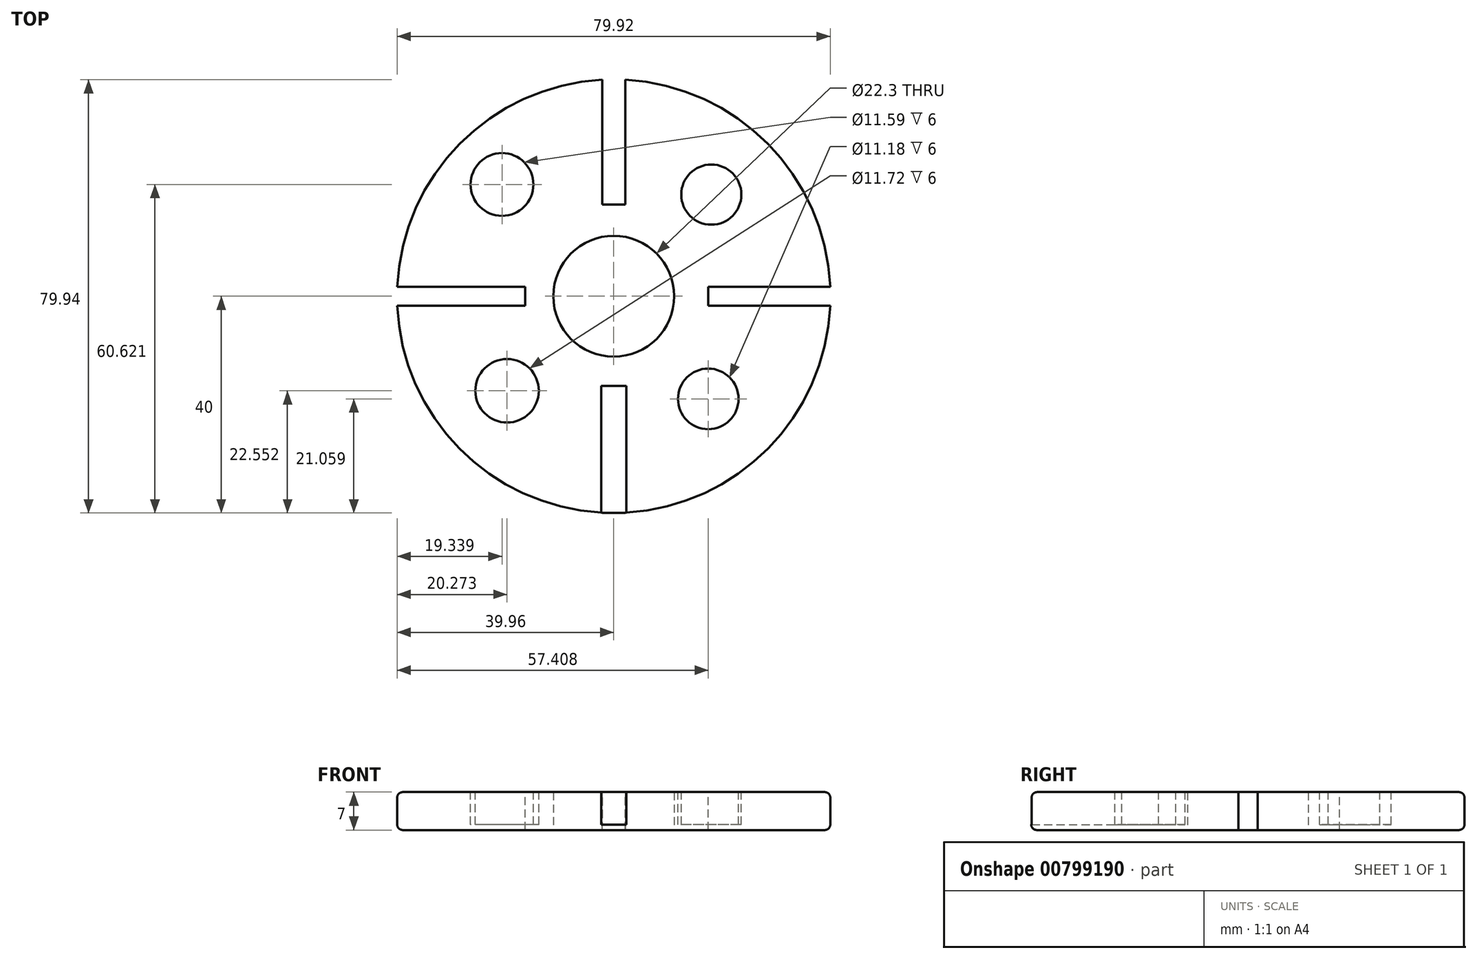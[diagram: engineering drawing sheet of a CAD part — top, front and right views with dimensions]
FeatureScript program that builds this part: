
annotation { "Feature Type Name" : "Feature", "Feature Type Description" : "" }
export const myFeature = defineFeature(function(context is Context, id is Id, definition is map)
    precondition{}
    {
        {
            var Q0;
            Q0=qCreatedBy(makeId("Top.planeOp"),FACE);
            var sketch = newSketch(context, id + "F0", { "sketchPlane" : qUnion([Q0])});
            skCircle(sketch, "E0", {"center": v(0, 0) * mm, "radius": 40 * mm});
            skCircle(sketch, "E1", {"center": v(0, 0) * mm, "radius": 11.15 * mm});
            skSolve(sketch);
        }
        {
            var Q0;
            Q0=makeQuery(id+"F0.imprint","IMPRINT",FACE,{"disambiguationData":[TD([[makeQuery(id+"F0.imprint","IMPRINT",EDGE,{"derivedFrom":sQuery(id+"F0.wireOp",EDGE,"E0")}),1.0]])]});
            extrude(context, id + "F1", {"entities" : qUnion([Q0]), "depth" : 7 * mm, "offsetDistance" : 25 * mm});
        }
        {
            var Q0;
            Q0=makeQuery(id+"F1.opExtrude","CAP_FACE",FACE,{"disambiguationData":[OSD([sQuery(id+"F0.wireOp",EDGE,"E0"),sQuery(id+"F0.wireOp",EDGE,"E1")])],"isStart":false});
            var sketch = newSketch(context, id + "F2", { "sketchPlane" : qUnion([Q0])});
            skSolve(sketch);
        }
        {
            var Q0;
            Q0=makeQuery(id+"F2.imprint","IMPRINT",FACE,{"disambiguationData":[TD([[makeQuery(id+"F2.imprint","IMPRINT",EDGE,{"derivedFrom":makeQuery(id+"F1.opExtrude","CAP_EDGE",EDGE,{"disambiguationData":[OSD([sQuery(id+"F0.wireOp",EDGE,"E0")])],"isStart":false})}),1.0]])]});
            var sketch = newSketch(context, id + "F3", { "sketchPlane" : qUnion([Q0])});
            skLineSegment(sketch, "E2.bottom", {"start": v(2.15, 16.89) * mm, "end": v(-2.15, 16.89) * mm});
            skLineSegment(sketch, "E2.top", {"start": v(2.15, 42.27) * mm, "end": v(-2.15, 42.27) * mm});
            skLineSegment(sketch, "E2.left", {"start": v(2.15, 16.89) * mm, "end": v(2.15, 42.27) * mm});
            skLineSegment(sketch, "E2.right", {"start": v(-2.15, 16.89) * mm, "end": v(-2.15, 42.27) * mm});
            skPoint(sketch, "E2.middle", {"position": v(0, 29.58) * mm});
            skSolve(sketch);
        }
        {
            var Q0;
            Q0 = qSketchRegion(id + "F3", true);
            extrude(context, id + "F4", {"entities" : qUnion([Q0]), "operationType" : NewBodyOperationType.REMOVE, "oppositeDirection" : true, "depth" : 50 * mm, "offsetDistance" : 25 * mm});
        }
        {
            var Q0;
            Q0=makeQuery(id+"F2.imprint","IMPRINT",FACE,{"disambiguationData":[TD([[makeQuery(id+"F2.imprint","IMPRINT",EDGE,{"derivedFrom":makeQuery(id+"F1.opExtrude","CAP_EDGE",EDGE,{"disambiguationData":[OSD([sQuery(id+"F0.wireOp",EDGE,"E0")])],"isStart":false})}),1.0]])]});
            var sketch = newSketch(context, id + "F5", { "sketchPlane" : qUnion([Q0])});
            skLineSegment(sketch, "E3.bottom", {"start": v(-16.33, -1.77) * mm, "end": v(-54.77, -1.77) * mm});
            skLineSegment(sketch, "E3.top", {"start": v(-16.33, 1.77) * mm, "end": v(-54.77, 1.77) * mm});
            skLineSegment(sketch, "E3.left", {"start": v(-16.33, -1.77) * mm, "end": v(-16.33, 1.77) * mm});
            skLineSegment(sketch, "E3.right", {"start": v(-54.77, -1.77) * mm, "end": v(-54.77, 1.77) * mm});
            skPoint(sketch, "E3.middle", {"position": v(-35.55, 0) * mm});
            skSolve(sketch);
        }
        {
            var Q0;
            Q0 = qSketchRegion(id + "F5", true);
            extrude(context, id + "F6", {"entities" : qUnion([Q0]), "operationType" : NewBodyOperationType.REMOVE, "oppositeDirection" : true, "depth" : 25 * mm, "offsetDistance" : 25 * mm});
        }
        {
            var Q0;
            Q0=makeQuery(id+"F2.imprint","IMPRINT",FACE,{"disambiguationData":[TD([[makeQuery(id+"F2.imprint","IMPRINT",EDGE,{"derivedFrom":makeQuery(id+"F1.opExtrude","CAP_EDGE",EDGE,{"disambiguationData":[OSD([sQuery(id+"F0.wireOp",EDGE,"E0")])],"isStart":false})}),1.0]])]});
            var sketch = newSketch(context, id + "F7", { "sketchPlane" : qUnion([Q0])});
            skLineSegment(sketch, "E4.bottom", {"start": v(2.33, -55.7) * mm, "end": v(-2.33, -55.7) * mm});
            skLineSegment(sketch, "E4.top", {"start": v(2.33, -16.52) * mm, "end": v(-2.33, -16.52) * mm});
            skLineSegment(sketch, "E4.left", {"start": v(2.33, -55.7) * mm, "end": v(2.33, -16.52) * mm});
            skLineSegment(sketch, "E4.right", {"start": v(-2.33, -55.7) * mm, "end": v(-2.33, -16.52) * mm});
            skPoint(sketch, "E4.middle", {"position": v(0, -36.1) * mm});
            skSolve(sketch);
        }
        {
            var Q0;
            Q0=makeQuery(id+"F2.imprint","IMPRINT",FACE,{"disambiguationData":[TD([[makeQuery(id+"F2.imprint","IMPRINT",EDGE,{"derivedFrom":makeQuery(id+"F1.opExtrude","CAP_EDGE",EDGE,{"disambiguationData":[OSD([sQuery(id+"F0.wireOp",EDGE,"E0")])],"isStart":false})}),1.0]])]});
            var sketch = newSketch(context, id + "F8", { "sketchPlane" : qUnion([Q0])});
            skLineSegment(sketch, "E5.bottom", {"start": v(46.93, -1.77) * mm, "end": v(17.45, -1.77) * mm});
            skLineSegment(sketch, "E5.top", {"start": v(46.93, 1.77) * mm, "end": v(17.45, 1.77) * mm});
            skLineSegment(sketch, "E5.left", {"start": v(46.93, -1.77) * mm, "end": v(46.93, 1.77) * mm});
            skLineSegment(sketch, "E5.right", {"start": v(17.45, -1.77) * mm, "end": v(17.45, 1.77) * mm});
            skPoint(sketch, "E5.middle", {"position": v(32.2, 0) * mm});
            skSolve(sketch);
        }
        {
            var Q0;
            Q0 = qSketchRegion(id + "F8", true);
            extrude(context, id + "F9", {"entities" : qUnion([Q0]), "operationType" : NewBodyOperationType.REMOVE, "oppositeDirection" : true, "depth" : 25 * mm, "offsetDistance" : 25 * mm});
        }
        {
            var Q0;
            Q0=makeQuery(id+"F2.imprint","IMPRINT",FACE,{"disambiguationData":[TD([[makeQuery(id+"F2.imprint","IMPRINT",EDGE,{"derivedFrom":makeQuery(id+"F1.opExtrude","CAP_EDGE",EDGE,{"disambiguationData":[OSD([sQuery(id+"F0.wireOp",EDGE,"E0")])],"isStart":false})}),1.0]])]});
            var sketch = newSketch(context, id + "F10", { "sketchPlane" : qUnion([Q0])});
            skCircle(sketch, "E6", {"center": v(-19.69, -17.45) * mm, "radius": 5.86 * mm});
            skCircle(sketch, "E7", {"center": v(-20.62, 20.62) * mm, "radius": 5.8 * mm});
            skSolve(sketch);
        }
        {
            var Q0;
            Q0=makeQuery(id+"F2.imprint","IMPRINT",FACE,{"disambiguationData":[TD([[makeQuery(id+"F2.imprint","IMPRINT",EDGE,{"derivedFrom":makeQuery(id+"F1.opExtrude","CAP_EDGE",EDGE,{"disambiguationData":[OSD([sQuery(id+"F0.wireOp",EDGE,"E0")])],"isStart":false})}),1.0]])]});
            var sketch = newSketch(context, id + "F11", { "sketchPlane" : qUnion([Q0])});
            skCircle(sketch, "E8", {"center": v(18, 18.75) * mm, "radius": 5.55 * mm});
            skCircle(sketch, "E9", {"center": v(17.45, -18.94) * mm, "radius": 5.6 * mm});
            skSolve(sketch);
        }
        {
            var Q0;
            {var subQ0=sQuery(id+"F0.wireOp",EDGE,"E0");Q0=makeQuery(id+"F6.boolean.opBoolean","SPLIT",EDGE,{"disambiguationData":[TD([makeQuery(id+"F4.boolean.opBoolean","COPY",FACE,{"derivedFrom":makeQuery(id+"F4.opExtrude","SWEPT_FACE",FACE,{"disambiguationData":[OSD([sQuery(id+"F3.wireOp",EDGE,"E2.right")])]})})])],"derivedFrom":makeQuery(id+"F1.opExtrude","CAP_EDGE",EDGE,{"disambiguationData":[OSD([subQ0])],"isStart":false})});}
            var Q1;
            {var subQ0=sQuery(id+"F0.wireOp",EDGE,"E0");Q1=makeQuery(id+"F6.boolean.opBoolean","SPLIT",EDGE,{"disambiguationData":[TD([makeQuery(id+"F4.boolean.opBoolean","COPY",FACE,{"derivedFrom":makeQuery(id+"F4.opExtrude","SWEPT_FACE",FACE,{"disambiguationData":[OSD([sQuery(id+"F3.wireOp",EDGE,"E2.right")])]})})])],"derivedFrom":makeQuery(id+"F1.opExtrude","CAP_EDGE",EDGE,{"disambiguationData":[OSD([subQ0])],"isStart":true})});}
            var Q2;
            {var subQ0=sQuery(id+"F0.wireOp",EDGE,"E0");var subQ3=makeQuery(id+"F4.boolean.opBoolean","COPY",FACE,{"derivedFrom":makeQuery(id+"F4.opExtrude","SWEPT_FACE",FACE,{"disambiguationData":[OSD([sQuery(id+"F3.wireOp",EDGE,"E2.left")])]})});Q2=makeQuery(id+"F9.boolean.opBoolean","SPLIT",EDGE,{"disambiguationData":[TD([subQ3])],"derivedFrom":makeQuery(id+"FT35M04vJGL3mYK_1.boolean.opBoolean","SPLIT",EDGE,{"disambiguationData":[TD([subQ3])],"derivedFrom":makeQuery(id+"F6.boolean.opBoolean","SPLIT",EDGE,{"disambiguationData":[TD([subQ3])],"derivedFrom":makeQuery(id+"F1.opExtrude","CAP_EDGE",EDGE,{"disambiguationData":[OSD([subQ0])],"isStart":true})})})});}
            var Q3;
            {var subQ0=sQuery(id+"F0.wireOp",EDGE,"E0");var subQ3=makeQuery(id+"F4.boolean.opBoolean","COPY",FACE,{"derivedFrom":makeQuery(id+"F4.opExtrude","SWEPT_FACE",FACE,{"disambiguationData":[OSD([sQuery(id+"F3.wireOp",EDGE,"E2.left")])]})});Q3=makeQuery(id+"F9.boolean.opBoolean","SPLIT",EDGE,{"disambiguationData":[TD([subQ3])],"derivedFrom":makeQuery(id+"FT35M04vJGL3mYK_1.boolean.opBoolean","SPLIT",EDGE,{"disambiguationData":[TD([subQ3])],"derivedFrom":makeQuery(id+"F6.boolean.opBoolean","SPLIT",EDGE,{"disambiguationData":[TD([subQ3])],"derivedFrom":makeQuery(id+"F1.opExtrude","CAP_EDGE",EDGE,{"disambiguationData":[OSD([subQ0])],"isStart":false})})})});}
            var Q4;
            {var subQ0=sQuery(id+"F0.wireOp",EDGE,"E0");var subQ2=makeQuery(id+"FT35M04vJGL3mYK_1.opExtrude","SWEPT_FACE",FACE,{"disambiguationData":[OSD([sQuery(id+"F7.wireOp",EDGE,"E4.left")])]});var subQ4=makeQuery(id+"F4.boolean.opBoolean","COPY",FACE,{"derivedFrom":makeQuery(id+"F4.opExtrude","SWEPT_FACE",FACE,{"disambiguationData":[OSD([sQuery(id+"F3.wireOp",EDGE,"E2.left")])]})});Q4=makeQuery(id+"F9.boolean.opBoolean","SPLIT",EDGE,{"disambiguationData":[TD([makeQuery(id+"FT35M04vJGL3mYK_1.boolean.opBoolean","COPY",FACE,{"derivedFrom":subQ2})])],"derivedFrom":makeQuery(id+"FT35M04vJGL3mYK_1.boolean.opBoolean","SPLIT",EDGE,{"disambiguationData":[TD([subQ4])],"derivedFrom":makeQuery(id+"F6.boolean.opBoolean","SPLIT",EDGE,{"disambiguationData":[TD([subQ4])],"derivedFrom":makeQuery(id+"F1.opExtrude","CAP_EDGE",EDGE,{"disambiguationData":[OSD([subQ0])],"isStart":false})})})});}
            var Q5;
            {var subQ0=sQuery(id+"F0.wireOp",EDGE,"E0");var subQ2=makeQuery(id+"F6.opExtrude","SWEPT_FACE",FACE,{"disambiguationData":[OSD([sQuery(id+"F5.wireOp",EDGE,"E3.bottom")])]});Q5=makeQuery(id+"FT35M04vJGL3mYK_1.boolean.opBoolean","SPLIT",EDGE,{"disambiguationData":[TD([makeQuery(id+"F6.boolean.opBoolean","COPY",FACE,{"derivedFrom":subQ2})])],"derivedFrom":makeQuery(id+"F6.boolean.opBoolean","SPLIT",EDGE,{"disambiguationData":[TD([makeQuery(id+"F4.boolean.opBoolean","COPY",FACE,{"derivedFrom":makeQuery(id+"F4.opExtrude","SWEPT_FACE",FACE,{"disambiguationData":[OSD([sQuery(id+"F3.wireOp",EDGE,"E2.left")])]})})])],"derivedFrom":makeQuery(id+"F1.opExtrude","CAP_EDGE",EDGE,{"disambiguationData":[OSD([subQ0])],"isStart":false})})});}
            var Q6;
            {var subQ0=sQuery(id+"F0.wireOp",EDGE,"E0");var subQ2=makeQuery(id+"F6.opExtrude","SWEPT_FACE",FACE,{"disambiguationData":[OSD([sQuery(id+"F5.wireOp",EDGE,"E3.bottom")])]});Q6=makeQuery(id+"FT35M04vJGL3mYK_1.boolean.opBoolean","SPLIT",EDGE,{"disambiguationData":[TD([makeQuery(id+"F6.boolean.opBoolean","COPY",FACE,{"derivedFrom":subQ2})])],"derivedFrom":makeQuery(id+"F6.boolean.opBoolean","SPLIT",EDGE,{"disambiguationData":[TD([makeQuery(id+"F4.boolean.opBoolean","COPY",FACE,{"derivedFrom":makeQuery(id+"F4.opExtrude","SWEPT_FACE",FACE,{"disambiguationData":[OSD([sQuery(id+"F3.wireOp",EDGE,"E2.left")])]})})])],"derivedFrom":makeQuery(id+"F1.opExtrude","CAP_EDGE",EDGE,{"disambiguationData":[OSD([subQ0])],"isStart":true})})});}
            var Q7;
            {var subQ0=sQuery(id+"F0.wireOp",EDGE,"E0");var subQ2=makeQuery(id+"FT35M04vJGL3mYK_1.opExtrude","SWEPT_FACE",FACE,{"disambiguationData":[OSD([sQuery(id+"F7.wireOp",EDGE,"E4.left")])]});var subQ4=makeQuery(id+"F4.boolean.opBoolean","COPY",FACE,{"derivedFrom":makeQuery(id+"F4.opExtrude","SWEPT_FACE",FACE,{"disambiguationData":[OSD([sQuery(id+"F3.wireOp",EDGE,"E2.left")])]})});Q7=makeQuery(id+"F9.boolean.opBoolean","SPLIT",EDGE,{"disambiguationData":[TD([makeQuery(id+"FT35M04vJGL3mYK_1.boolean.opBoolean","COPY",FACE,{"derivedFrom":subQ2})])],"derivedFrom":makeQuery(id+"FT35M04vJGL3mYK_1.boolean.opBoolean","SPLIT",EDGE,{"disambiguationData":[TD([subQ4])],"derivedFrom":makeQuery(id+"F6.boolean.opBoolean","SPLIT",EDGE,{"disambiguationData":[TD([subQ4])],"derivedFrom":makeQuery(id+"F1.opExtrude","CAP_EDGE",EDGE,{"disambiguationData":[OSD([subQ0])],"isStart":true})})})});}
            fillet(context, id + "F12", {"entities" : qUnion([Q0, Q1, Q2, Q3, Q4, Q5, Q6, Q7]), "radius" : 1 * mm, "tangentPropagation" : true, "allowEdgeOverflow" : false});
        }
        {
            var Q0;
            {var subQ0=sQuery(id+"F7.wireOp",EDGE,"E4.top");Q0=makeQuery(id+"F7.imprint","IMPRINT",FACE,{"disambiguationData":[TD([[makeQuery(id+"F7.imprint","IMPRINT",EDGE,{"derivedFrom":subQ0}),1.0]])]});}
            extrude(context, id + "F13", {"entities" : qUnion([Q0]), "operationType" : NewBodyOperationType.REMOVE, "oppositeDirection" : true, "depth" : 6 * mm, "offsetDistance" : 25 * mm});
        }
        {
            var Q0;
            Q0=makeQuery(id+"F10.imprint","IMPRINT",FACE,{"disambiguationData":[TD([[makeQuery(id+"F10.imprint","IMPRINT",EDGE,{"derivedFrom":sQuery(id+"F10.wireOp",EDGE,"E7")}),1.0]])]});
            var Q1;
            Q1=makeQuery(id+"F10.imprint","IMPRINT",FACE,{"disambiguationData":[TD([[makeQuery(id+"F10.imprint","IMPRINT",EDGE,{"derivedFrom":sQuery(id+"F10.wireOp",EDGE,"E6")}),1.0]])]});
            var Q2;
            Q2=makeQuery(id+"F11.imprint","IMPRINT",FACE,{"disambiguationData":[TD([[makeQuery(id+"F11.imprint","IMPRINT",EDGE,{"derivedFrom":sQuery(id+"F11.wireOp",EDGE,"E8")}),1.0]])]});
            var Q3;
            Q3=makeQuery(id+"F11.imprint","IMPRINT",FACE,{"disambiguationData":[TD([[makeQuery(id+"F11.imprint","IMPRINT",EDGE,{"derivedFrom":sQuery(id+"F11.wireOp",EDGE,"E9")}),1.0]])]});
            extrude(context, id + "F14", {"entities" : qUnion([Q0, Q1, Q2, Q3]), "operationType" : NewBodyOperationType.REMOVE, "oppositeDirection" : true, "depth" : 6 * mm, "offsetDistance" : 25 * mm});
        }
    });
